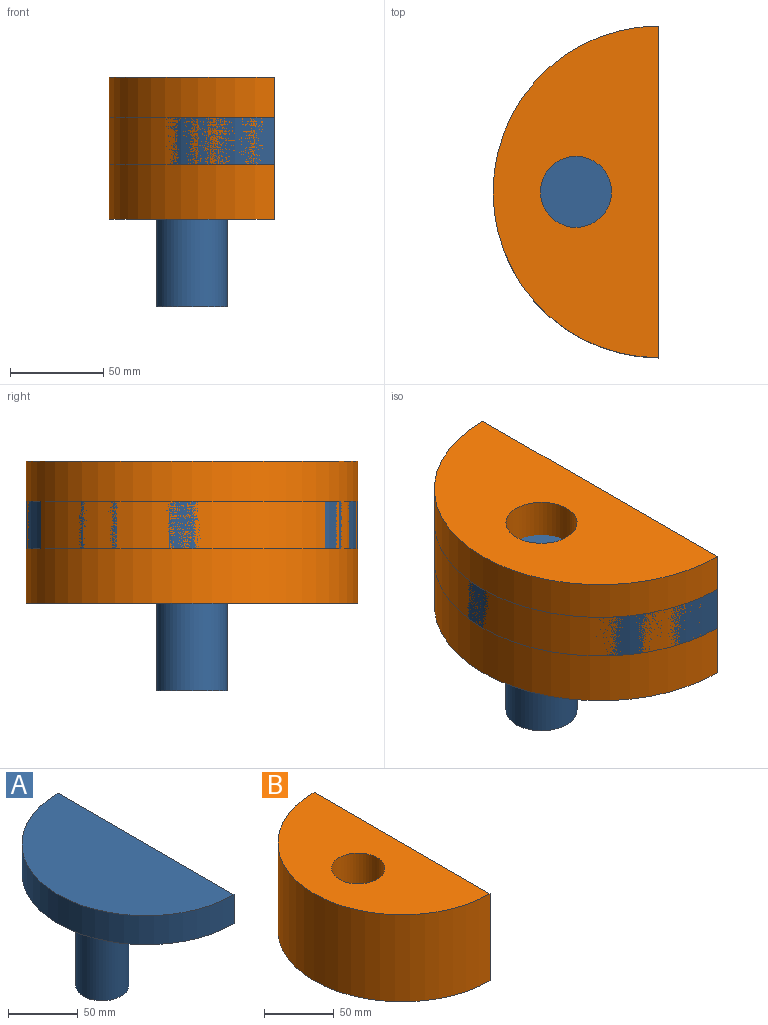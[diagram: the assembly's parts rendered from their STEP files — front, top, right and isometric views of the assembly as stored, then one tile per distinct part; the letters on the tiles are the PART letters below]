
ASSEMBLY  parts=2 mates=1
PART A: 6 faces, bbox 88.9x177.8x101.6 mm
  f0: plane 177.8x25.4mm, normal (1,0,0), area 4516.1mm2, adj f1,f2,f3
  f1: cylinder r=88.9mm len=177.8mm, axis (0,0,-1), area 7093.9mm2, adj f0,f2,f3
  f2: plane 177.8x88.9mm, normal (0,0,1), area 12414.3mm2, adj f0,f1
  f3: plane 177.8x88.9mm, normal (0,0,-1), area 11274.2mm2, adj f0,f1,f4
  f4: cylinder r=19.05mm len=76.2mm, axis (0,0,1), area 9120.7mm2, adj f3,f5
  f5: plane 38.1x38.1mm, normal (0,0,-1), area 1140.1mm2, adj f4
PART B: 5 faces, bbox 88.9x177.8x76.2 mm
  f0: plane 177.8x76.2mm, normal (1,0,0), area 13548.4mm2, adj f1,f3,f4
  f1: cylinder r=88.9mm len=177.8mm, axis (0,0,-1), area 21281.7mm2, adj f0,f3,f4
  f2: cylinder r=19.05mm len=76.2mm, axis (0,0,-1), area 9120.7mm2, adj f3,f4
  f3: plane 177.8x88.9mm, normal (0,0,1), area 11274.2mm2, adj f0,f1,f2
  f4: plane 177.8x88.9mm, normal (0,0,-1), area 11274.2mm2, adj f0,f1,f2
PLACE A rot(axis=(0,0,-1),0deg) t=(-93.98,-106.68,-35.01)mm
PLACE B rot(axis=(0,0,-1),0deg) t=(-93.98,-106.68,-64.36)mm
MATE slider A.f4 <-> B.f2  axis (0,0,-1) through (-138.43,-106.68,-111.21)mm
